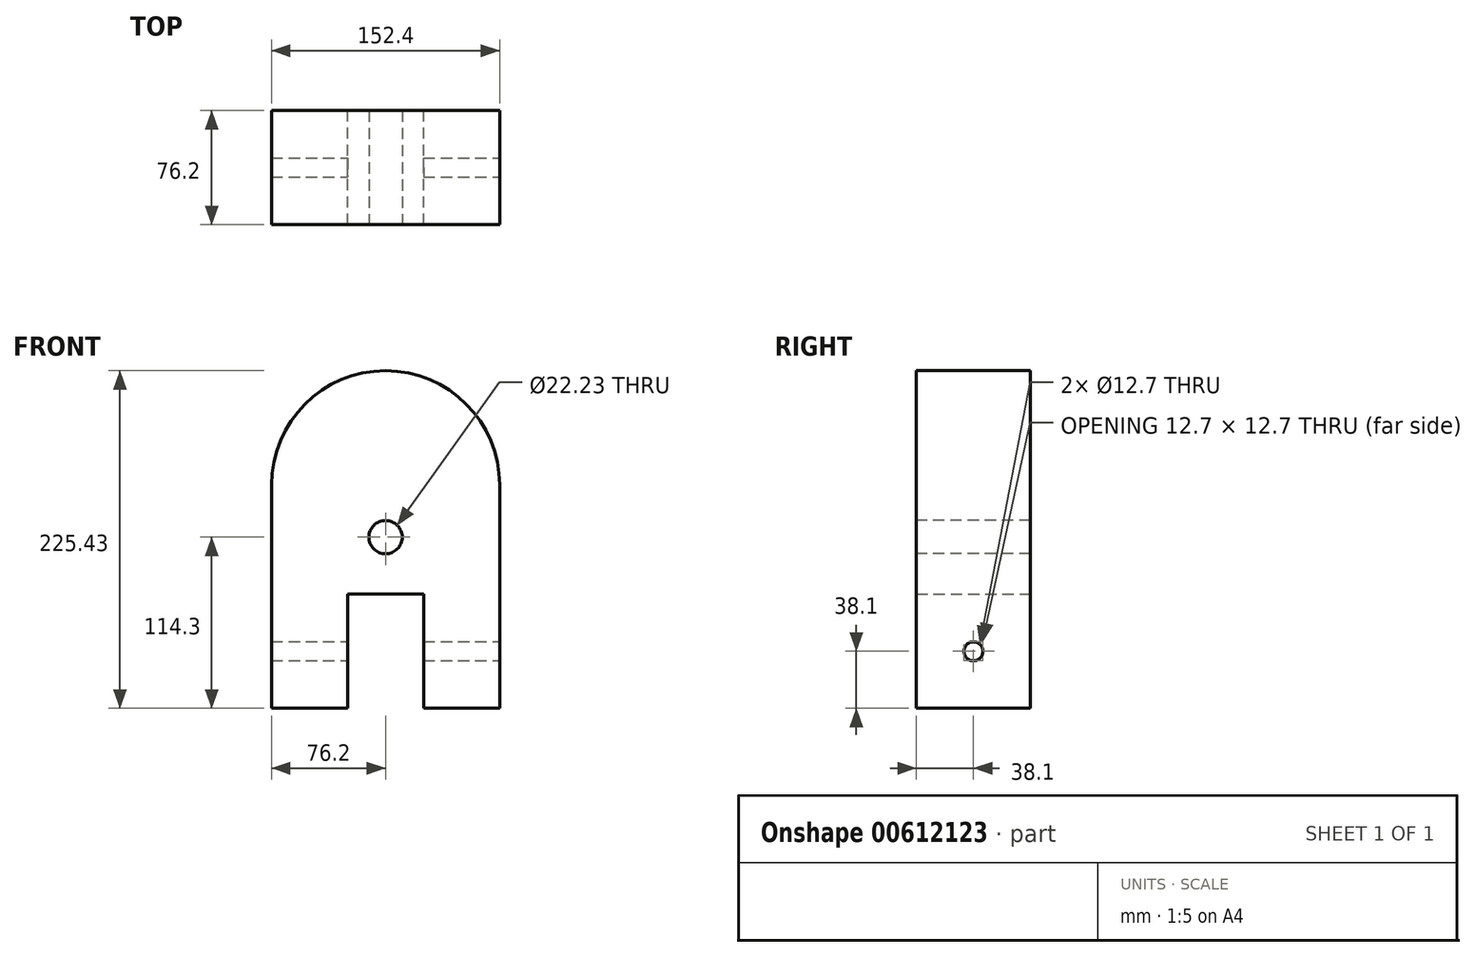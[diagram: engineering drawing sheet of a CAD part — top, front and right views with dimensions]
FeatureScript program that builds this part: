
annotation { "Feature Type Name" : "Feature", "Feature Type Description" : "" }
export const myFeature = defineFeature(function(context is Context, id is Id, definition is map)
    precondition{}
    {
        {
            var Q0;
            Q0=qCreatedBy(makeId("Front.planeOp"),FACE);
            var sketch = newSketch(context, id + "F0", { "sketchPlane" : qUnion([Q0])});
            skLineSegment(sketch, "E0", {"start": v(0, 0) * mm, "end": v(-50.8, 0) * mm});
            skLineSegment(sketch, "E1", {"start": v(-50.8, 0) * mm, "end": v(-50.8, 225.42) * mm});
            skLineSegment(sketch, "E2", {"start": v(101.6, 225.43) * mm, "end": v(101.6, 0) * mm});
            skLineSegment(sketch, "E3", {"start": v(101.6, 0) * mm, "end": v(50.8, 0) * mm});
            skLineSegment(sketch, "E4", {"start": v(50.8, 0) * mm, "end": v(50.8, 76.2) * mm});
            skLineSegment(sketch, "E5", {"start": v(50.8, 76.2) * mm, "end": v(0, 76.2) * mm});
            skLineSegment(sketch, "E6", {"start": v(0, 76.2) * mm, "end": v(0, 0) * mm});
            skLineSegment(sketch, "E7", {"start": v(-50.8, 225.42) * mm, "end": v(101.6, 225.42) * mm});
            skSolve(sketch);
        }
        {
            var Q0;
            Q0=makeQuery(id+"F0.imprint","IMPRINT",FACE,{"disambiguationData":[TD([[makeQuery(id+"F0.imprint","IMPRINT",EDGE,{"derivedFrom":sQuery(id+"F0.wireOp",EDGE,"E0")}),-1.0]])]});
            extrude(context, id + "F1", {"entities" : qUnion([Q0]), "depth" : 76.2 * mm, "offsetDistance" : 25.4 * mm});
        }
        {
            var Q0;
            Q0=makeQuery(id+"F1.opExtrude","SWEPT_EDGE",EDGE,{"disambiguationData":[OSD([sQuery(id+"F0.wireOp",EDGE,"E2"),sQuery(id+"F0.wireOp",EDGE,"E7")])]});
            var Q1;
            Q1=makeQuery(id+"F1.opExtrude","SWEPT_EDGE",EDGE,{"disambiguationData":[OSD([sQuery(id+"F0.wireOp",EDGE,"E1"),sQuery(id+"F0.wireOp",EDGE,"E7")])]});
            fillet(context, id + "F2", {"entities" : qUnion([Q0, Q1]), "radius" : 76.2 * mm, "tangentPropagation" : true, "allowEdgeOverflow" : false});
        }
        {
            var Q0;
            Q0=makeQuery(id+"F1.opExtrude","CAP_FACE",FACE,{"disambiguationData":[OSD([sQuery(id+"F0.wireOp",EDGE,"E0"),sQuery(id+"F0.wireOp",EDGE,"E1"),sQuery(id+"F0.wireOp",EDGE,"E2"),sQuery(id+"F0.wireOp",EDGE,"E3"),sQuery(id+"F0.wireOp",EDGE,"E4"),sQuery(id+"F0.wireOp",EDGE,"E5"),sQuery(id+"F0.wireOp",EDGE,"E6"),sQuery(id+"F0.wireOp",EDGE,"E7")])],"isStart":false});
            var sketch = newSketch(context, id + "F3", { "sketchPlane" : qUnion([Q0])});
            skCircle(sketch, "E8", {"center": v(25.4, 114.3) * mm, "radius": 11.11 * mm});
            skSolve(sketch);
        }
        {
            var Q0;
            Q0=sQuery(id+"F3.wireOp",VERTEX,"E8.center");
            var Q1;
            Q1=makeQuery(id+"F1.opExtrude","SWEPT_BODY",BODY,{"disambiguationData":[OSD([sQuery(id+"F0.wireOp",EDGE,"E0"),sQuery(id+"F0.wireOp",EDGE,"E1"),sQuery(id+"F0.wireOp",EDGE,"E2"),sQuery(id+"F0.wireOp",EDGE,"E3"),sQuery(id+"F0.wireOp",EDGE,"E4"),sQuery(id+"F0.wireOp",EDGE,"E5"),sQuery(id+"F0.wireOp",EDGE,"E6"),sQuery(id+"F0.wireOp",EDGE,"E7")])]});
            hole(context, id + "F4", {"style" : HoleStyle.SIMPLE, "endStyle" : HoleEndStyle.THROUGH, "holeDiameter" : 22.22 * mm, "majorDiameter" : 6.35 * mm, "isTappedThrough" : true, "tappedDepth" : 12.7 * mm, "tapClearance" : 3, "locations" : qUnion([Q0]), "scope" : qUnion([Q1])});
        }
        {
            var Q0;
            Q0=makeQuery(id+"F1.opExtrude","SWEPT_FACE",FACE,{"disambiguationData":[OSD([sQuery(id+"F0.wireOp",EDGE,"E2")])]});
            var sketch = newSketch(context, id + "F5", { "sketchPlane" : qUnion([Q0])});
            skCircle(sketch, "E9", {"center": v(-38.1, 38.1) * mm, "radius": 6.35 * mm});
            skSolve(sketch);
        }
        {
            var Q0;
            Q0=sQuery(id+"F5.wireOp",VERTEX,"E9.center");
            var Q1;
            Q1=makeQuery(id+"F1.opExtrude","SWEPT_BODY",BODY,{"disambiguationData":[OSD([sQuery(id+"F0.wireOp",EDGE,"E0"),sQuery(id+"F0.wireOp",EDGE,"E1"),sQuery(id+"F0.wireOp",EDGE,"E2"),sQuery(id+"F0.wireOp",EDGE,"E3"),sQuery(id+"F0.wireOp",EDGE,"E4"),sQuery(id+"F0.wireOp",EDGE,"E5"),sQuery(id+"F0.wireOp",EDGE,"E6"),sQuery(id+"F0.wireOp",EDGE,"E7")])]});
            hole(context, id + "F6", {"style" : HoleStyle.SIMPLE, "endStyle" : HoleEndStyle.THROUGH, "holeDiameter" : 12.7 * mm, "majorDiameter" : 6.35 * mm, "isTappedThrough" : true, "tappedDepth" : 12.7 * mm, "tapClearance" : 3, "locations" : qUnion([Q0]), "scope" : qUnion([Q1])});
        }
    });
